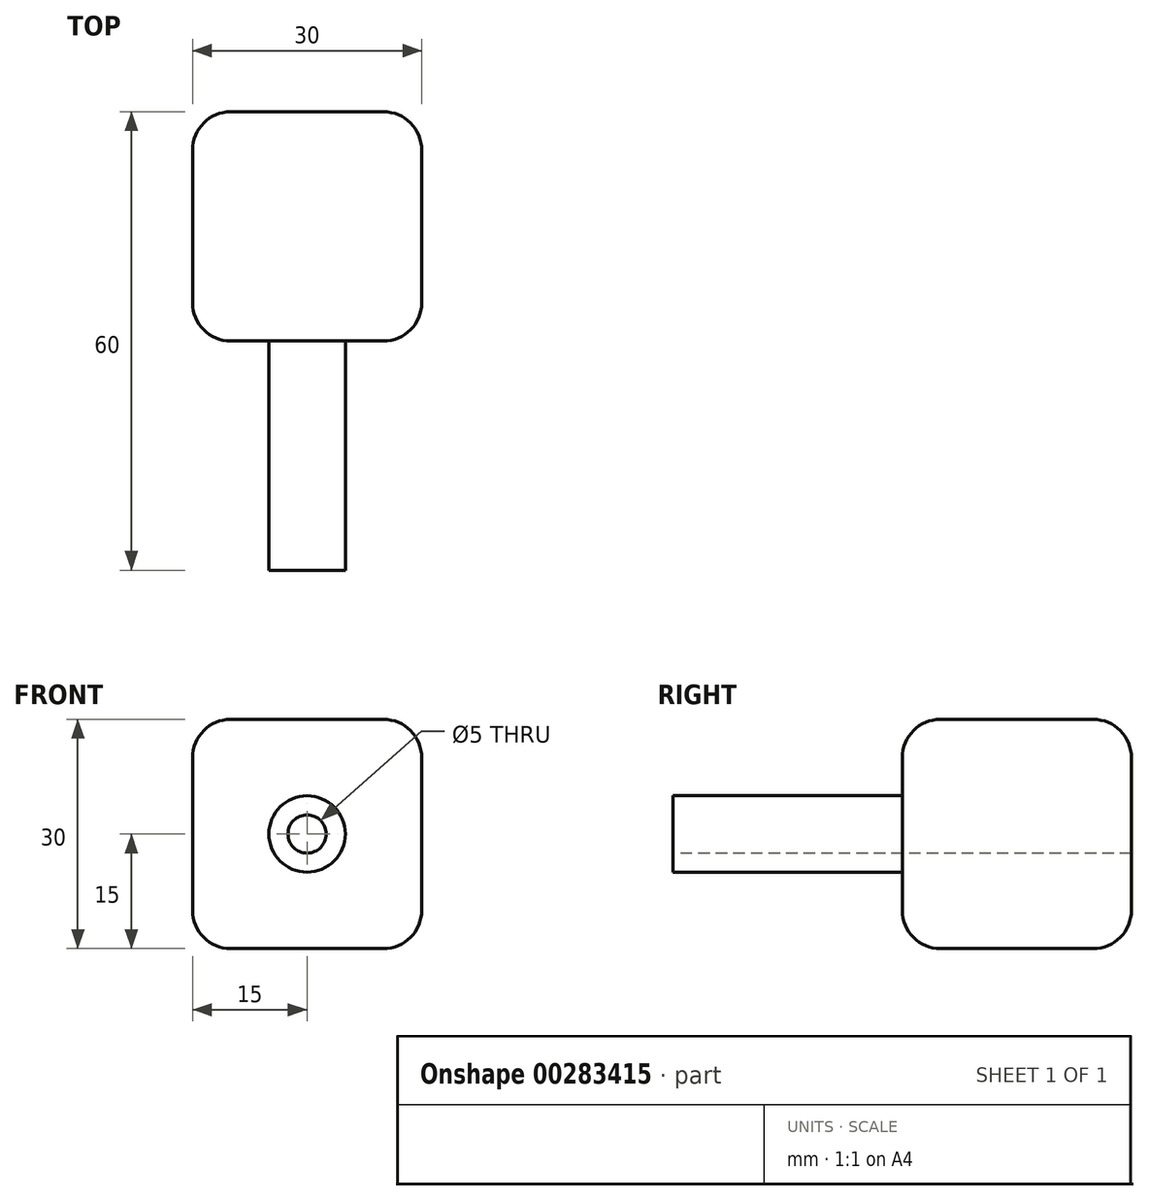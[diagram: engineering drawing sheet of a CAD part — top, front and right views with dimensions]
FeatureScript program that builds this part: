
annotation { "Feature Type Name" : "Feature", "Feature Type Description" : "" }
export const myFeature = defineFeature(function(context is Context, id is Id, definition is map)
    precondition{}
    {
        {
            var Q0;
            Q0=qCreatedBy(makeId("Front.planeOp"),FACE);
            var sketch = newSketch(context, id + "F0", { "sketchPlane" : qUnion([Q0])});
            skLineSegment(sketch, "E0.bottom", {"start": v(-15, 15) * mm, "end": v(15, 15) * mm});
            skLineSegment(sketch, "E0.top", {"start": v(-15, -15) * mm, "end": v(15, -15) * mm});
            skLineSegment(sketch, "E0.left", {"start": v(-15, 15) * mm, "end": v(-15, -15) * mm});
            skLineSegment(sketch, "E0.right", {"start": v(15, 15) * mm, "end": v(15, -15) * mm});
            skPoint(sketch, "E0.middle", {"position": v(0, 0) * mm});
            skSolve(sketch);
        }
        {
            var Q0;
            Q0 = qSketchRegion(id + "F0", true);
            extrude(context, id + "F1", {"entities" : qUnion([Q0]), "depth" : 30 * mm});
        }
        {
            var Q0;
            Q0=makeQuery(id+"F1.opExtrude","CAP_FACE",FACE,{"disambiguationData":[OSD([sQuery(id+"F0.wireOp",EDGE,"E0.bottom"),sQuery(id+"F0.wireOp",EDGE,"E0.top"),sQuery(id+"F0.wireOp",EDGE,"E0.left"),sQuery(id+"F0.wireOp",EDGE,"E0.right")])],"isStart":false});
            var sketch = newSketch(context, id + "F2", { "sketchPlane" : qUnion([Q0])});
            skCircle(sketch, "E1", {"center": v(0, 0) * mm, "radius": 5 * mm});
            skSolve(sketch);
        }
        {
            var Q0;
            Q0 = qSketchRegion(id + "F2", true);
            extrude(context, id + "F3", {"entities" : qUnion([Q0]), "operationType" : NewBodyOperationType.ADD, "depth" : 30 * mm});
        }
        {
            var Q0;
            Q0=makeQuery(id+"F3.opExtrude","CAP_FACE",FACE,{"disambiguationData":[OSD([sQuery(id+"F2.wireOp",EDGE,"E1")])],"isStart":false});
            var sketch = newSketch(context, id + "F4", { "sketchPlane" : qUnion([Q0])});
            skCircle(sketch, "E2", {"center": v(0, 0) * mm, "radius": 2.5 * mm});
            skSolve(sketch);
        }
        {
            var Q0;
            Q0=makeQuery(id+"F4.imprint","IMPRINT",FACE,{"disambiguationData":[TD([[makeQuery(id+"F4.imprint","IMPRINT",EDGE,{"derivedFrom":sQuery(id+"F4.wireOp",EDGE,"E2")}),1.0]])]});
            extrude(context, id + "F5", {"entities" : qUnion([Q0]), "operationType" : NewBodyOperationType.REMOVE, "endBound" : BoundingType.THROUGH_ALL, "oppositeDirection" : true, "depth" : 84.4 * mm});
        }
        {
            var Q0;
            Q0=makeQuery(id+"F1.opExtrude","SWEPT_EDGE",EDGE,{"disambiguationData":[OSD([sQuery(id+"F0.wireOp",EDGE,"E0.bottom"),sQuery(id+"F0.wireOp",EDGE,"E0.right")])]});
            var Q1;
            Q1=makeQuery(id+"F1.opExtrude","SWEPT_EDGE",EDGE,{"disambiguationData":[OSD([sQuery(id+"F0.wireOp",EDGE,"E0.bottom"),sQuery(id+"F0.wireOp",EDGE,"E0.left")])]});
            var Q2;
            Q2=makeQuery(id+"F1.opExtrude","CAP_EDGE",EDGE,{"disambiguationData":[OSD([sQuery(id+"F0.wireOp",EDGE,"E0.bottom")])],"isStart":false});
            var Q3;
            Q3=makeQuery(id+"F1.opExtrude","CAP_EDGE",EDGE,{"disambiguationData":[OSD([sQuery(id+"F0.wireOp",EDGE,"E0.bottom")])],"isStart":true});
            var Q4;
            Q4=makeQuery(id+"F1.opExtrude","CAP_EDGE",EDGE,{"disambiguationData":[OSD([sQuery(id+"F0.wireOp",EDGE,"E0.top")])],"isStart":false});
            var Q5;
            Q5=makeQuery(id+"F1.opExtrude","SWEPT_EDGE",EDGE,{"disambiguationData":[OSD([sQuery(id+"F0.wireOp",EDGE,"E0.top"),sQuery(id+"F0.wireOp",EDGE,"E0.left")])]});
            var Q6;
            Q6=makeQuery(id+"F1.opExtrude","SWEPT_EDGE",EDGE,{"disambiguationData":[OSD([sQuery(id+"F0.wireOp",EDGE,"E0.top"),sQuery(id+"F0.wireOp",EDGE,"E0.right")])]});
            var Q7;
            Q7=makeQuery(id+"F1.opExtrude","CAP_EDGE",EDGE,{"disambiguationData":[OSD([sQuery(id+"F0.wireOp",EDGE,"E0.top")])],"isStart":true});
            var Q8;
            Q8=makeQuery(id+"F5.boolean.opBoolean","COPY",EDGE,{"derivedFrom":makeQuery(id+"F5.opExtrude","CAP_EDGE",EDGE,{"disambiguationData":[OSD([sQuery(id+"F4.wireOp",EDGE,"E2")])],"isStart":true})});
            var Q9;
            Q9=makeQuery(id+"F1.opExtrude","SWEPT_FACE",FACE,{"disambiguationData":[OSD([sQuery(id+"F0.wireOp",EDGE,"E0.left")])]});
            var Q10;
            Q10=makeQuery(id+"F1.opExtrude","SWEPT_FACE",FACE,{"disambiguationData":[OSD([sQuery(id+"F0.wireOp",EDGE,"E0.right")])]});
            fillet(context, id + "F6", {"entities" : qUnion([Q0, Q1, Q2, Q3, Q4, Q5, Q6, Q7, Q8, Q9, Q10]), "radius" : 5 * mm, "tangentPropagation" : true, "allowEdgeOverflow" : false});
        }
    });
